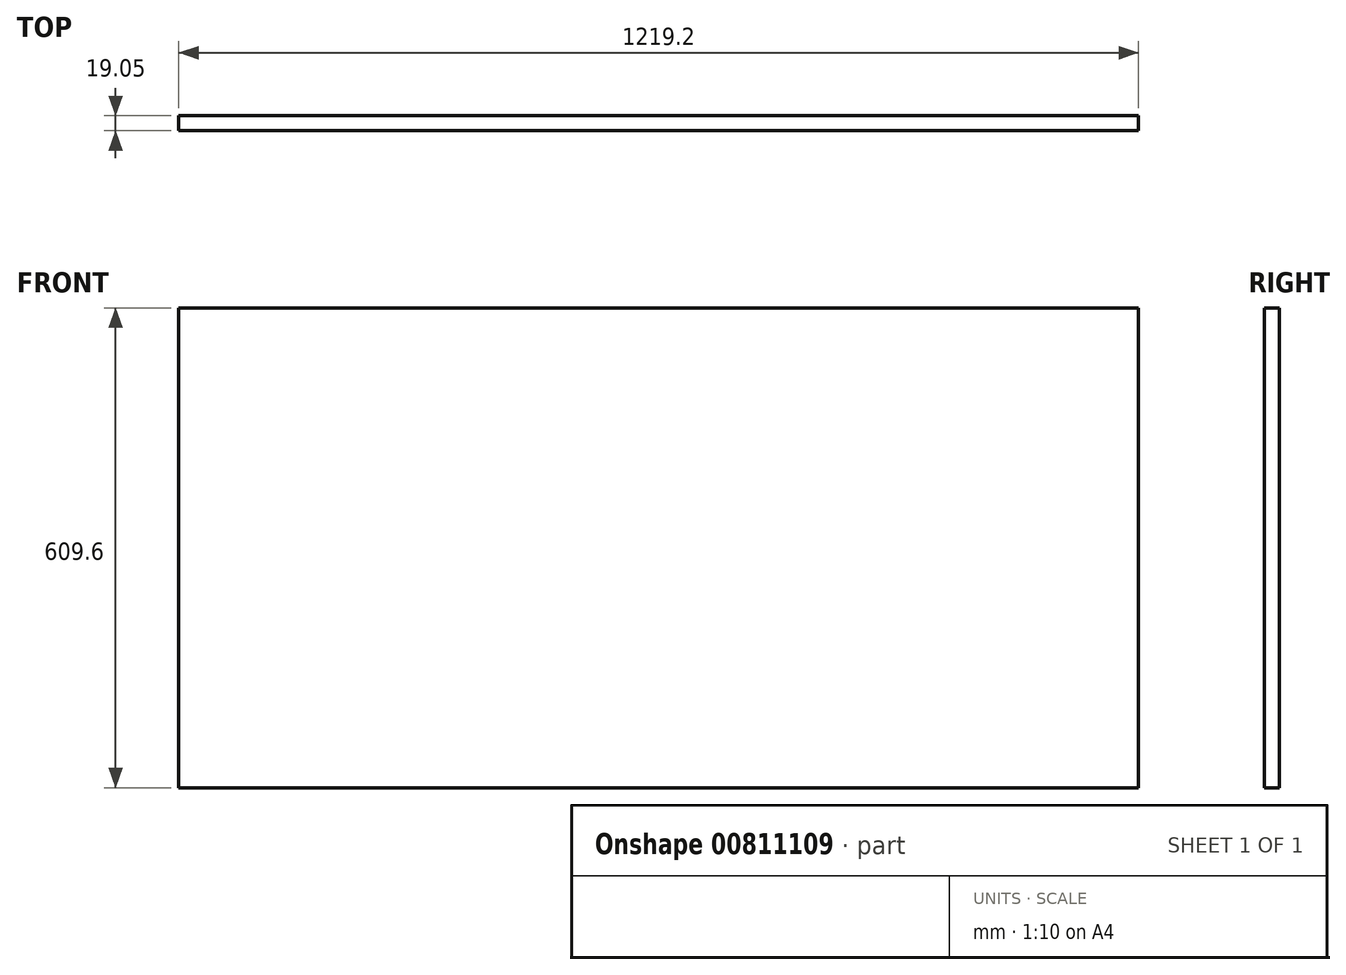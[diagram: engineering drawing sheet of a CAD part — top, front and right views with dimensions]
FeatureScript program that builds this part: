
annotation { "Feature Type Name" : "Feature", "Feature Type Description" : "" }
export const myFeature = defineFeature(function(context is Context, id is Id, definition is map)
    precondition{}
    {
        {
            var Q0;
            Q0=qCreatedBy(makeId("Front.planeOp"),FACE);
            var sketch = newSketch(context, id + "F0", { "sketchPlane" : qUnion([Q0])});
            skLineSegment(sketch, "E0.bottom", {"start": v(609.6, -304.8) * mm, "end": v(-609.6, -304.8) * mm});
            skLineSegment(sketch, "E0.top", {"start": v(609.6, 304.8) * mm, "end": v(-609.6, 304.8) * mm});
            skLineSegment(sketch, "E0.left", {"start": v(609.6, -304.8) * mm, "end": v(609.6, 304.8) * mm});
            skLineSegment(sketch, "E0.right", {"start": v(-609.6, -304.8) * mm, "end": v(-609.6, 304.8) * mm});
            skPoint(sketch, "E0.middle", {"position": v(0, 0) * mm});
            skSolve(sketch);
        }
        {
            var Q0;
            Q0=makeQuery(id+"F0.imprint","IMPRINT",FACE,{"disambiguationData":[TD([[makeQuery(id+"F0.imprint","IMPRINT",EDGE,{"derivedFrom":sQuery(id+"F0.wireOp",EDGE,"E0.bottom")}),-1.0]])]});
            extrude(context, id + "F1", {"entities" : qUnion([Q0]), "depth" : 19.05 * mm, "offsetDistance" : 25.4 * mm});
        }
    });
